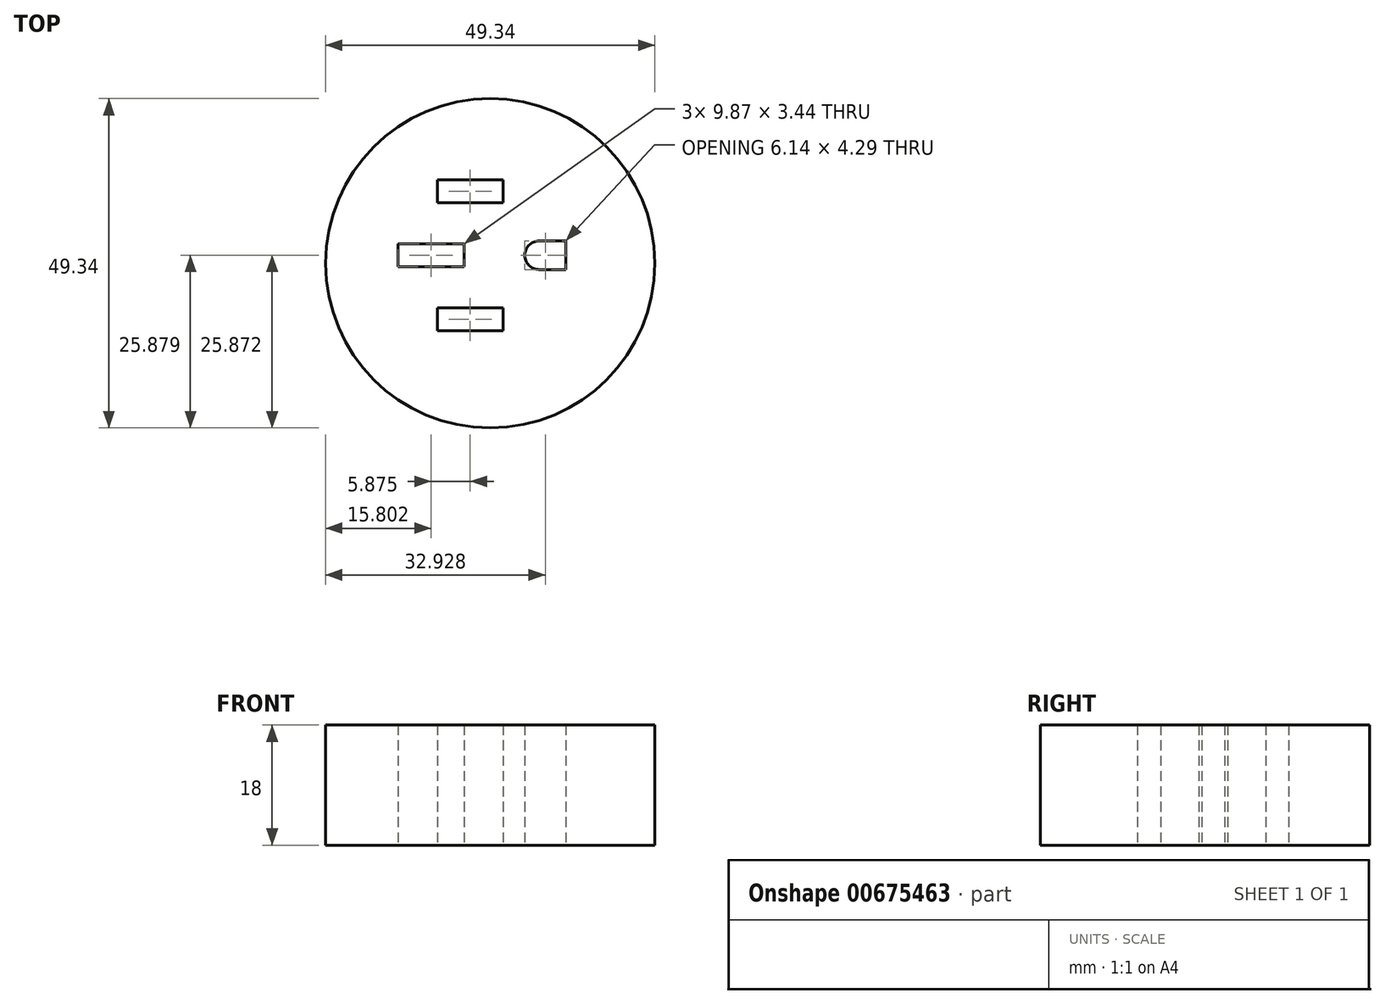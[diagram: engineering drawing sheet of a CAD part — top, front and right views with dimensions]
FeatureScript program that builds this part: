
annotation { "Feature Type Name" : "Feature", "Feature Type Description" : "" }
export const myFeature = defineFeature(function(context is Context, id is Id, definition is map)
    precondition{}
    {
        {
            var Q0;
            Q0=qCreatedBy(makeId("Top.planeOp"),FACE);
            var sketch = newSketch(context, id + "F0", { "sketchPlane" : qUnion([Q0])});
            skCircle(sketch, "E0", {"center": v(0, 0) * mm, "radius": 24.67 * mm});
            skLineSegment(sketch, "E1.bottom", {"start": v(-7.93, -10.13) * mm, "end": v(-7.93, -6.69) * mm});
            skLineSegment(sketch, "E1.top", {"start": v(1.94, -10.13) * mm, "end": v(1.94, -6.69) * mm});
            skLineSegment(sketch, "E1.left", {"start": v(-7.93, -10.13) * mm, "end": v(1.94, -10.13) * mm});
            skLineSegment(sketch, "E1.right", {"start": v(-7.93, -6.69) * mm, "end": v(1.94, -6.69) * mm});
            skLineSegment(sketch, "E2.MirrorCS", {"start": v(-13.8, -0.52) * mm, "end": v(-3.93, -0.52) * mm});
            skLineSegment(sketch, "E3.MirrorCS", {"start": v(-7.93, 9.1) * mm, "end": v(1.94, 9.1) * mm});
            skLineSegment(sketch, "E4.MirrorCS", {"start": v(-7.93, 12.53) * mm, "end": v(-7.93, 9.1) * mm});
            skLineSegment(sketch, "E5.MirrorCS", {"start": v(-7.93, 12.53) * mm, "end": v(1.94, 12.53) * mm});
            skLineSegment(sketch, "E6.MirrorCS", {"start": v(1.94, 12.53) * mm, "end": v(1.94, 9.1) * mm});
            skLineSegment(sketch, "E7.MirrorCS", {"start": v(-13.8, 2.92) * mm, "end": v(-3.93, 2.92) * mm});
            skLineSegment(sketch, "E8", {"start": v(-13.8, -0.52) * mm, "end": v(-13.8, 2.92) * mm});
            skLineSegment(sketch, "E9", {"start": v(-3.93, -0.52) * mm, "end": v(-3.93, 2.92) * mm});
            skLineSegment(sketch, "E10.bottom", {"start": v(11.33, -0.94) * mm, "end": v(11.33, 3.36) * mm});
            skLineSegment(sketch, "E10.left", {"start": v(11.33, -0.94) * mm, "end": v(7.33, -0.94) * mm});
            skLineSegment(sketch, "E10.right", {"start": v(11.33, 3.36) * mm, "end": v(7.33, 3.36) * mm});
            skArc(sketch, "E11", {"start": v(7.33, 3.36) * mm, "mid": v(5.19, 1.2) * mm, "end": v(7.33, -0.94) * mm});
            skSolve(sketch);
        }
        {
            var Q0;
            Q0 = qSketchRegion(id + "F0", true);
            extrude(context, id + "F1", {"entities" : qUnion([Q0]), "depth" : 18.8 * mm, "offsetDistance" : 25 * mm});
        }
        {
            var Q0;
            Q0 = qSketchRegion(id + "F0", true);
            var Q1;
            Q1=makeQuery(id+"F0.imprint","IMPRINT",FACE,{"disambiguationData":[TD([[makeQuery(id+"F0.imprint","IMPRINT",EDGE,{"derivedFrom":sQuery(id+"F0.wireOp",EDGE,"E1.bottom")}),-1.0]])]});
            var Q2;
            Q2=makeQuery(id+"F0.imprint","IMPRINT",FACE,{"disambiguationData":[TD([[makeQuery(id+"F0.imprint","IMPRINT",EDGE,{"derivedFrom":sQuery(id+"F0.wireOp",EDGE,"463338f3-baaf-430d-bb06-9a12d469661e0.MirrorCS")}),-1.0]])]});
            var Q3;
            Q3=makeQuery(id+"F0.imprint","IMPRINT",FACE,{"disambiguationData":[TD([[makeQuery(id+"F0.imprint","IMPRINT",EDGE,{"derivedFrom":sQuery(id+"F0.wireOp",EDGE,"8IOIInOe-9Ach-LeR5-Veee-tgPsVm3crWa1")}),1.0]])]});
            extrude(context, id + "F2", {"entities" : qUnion([Q0, Q1, Q2, Q3]), "operationType" : NewBodyOperationType.REMOVE, "depth" : 0.8 * mm, "offsetDistance" : 25 * mm});
        }
    });
